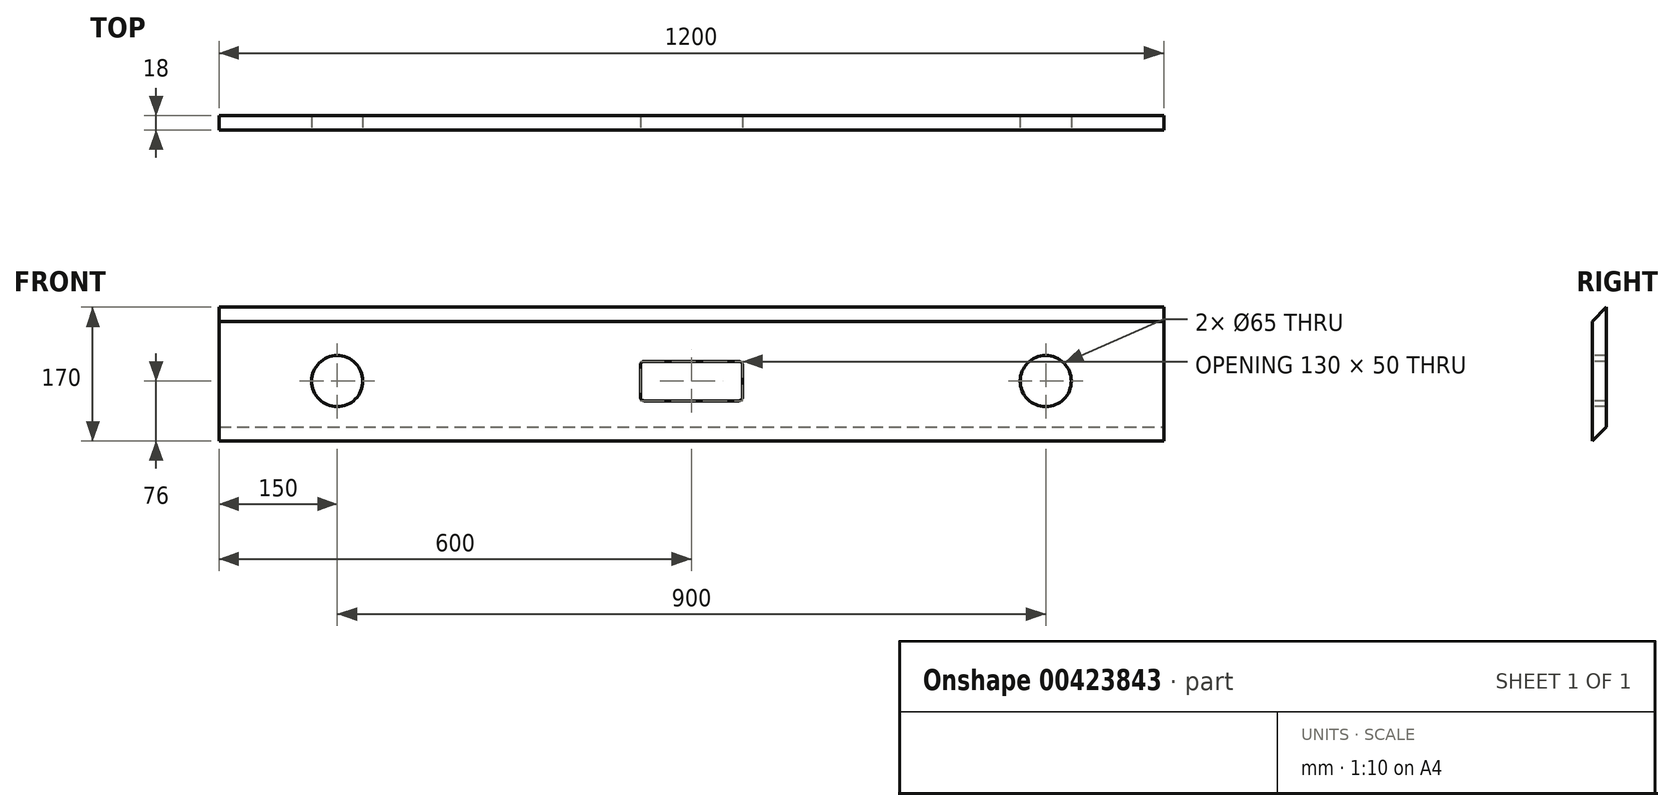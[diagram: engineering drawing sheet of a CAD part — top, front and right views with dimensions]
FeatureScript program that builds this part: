
annotation { "Feature Type Name" : "Feature", "Feature Type Description" : "" }
export const myFeature = defineFeature(function(context is Context, id is Id, definition is map)
    precondition{}
    {
        {
            var Q0;
            Q0=qCreatedBy(makeId("Front.planeOp"),FACE);
            var sketch = newSketch(context, id + "F0", { "sketchPlane" : qUnion([Q0])});
            skLineSegment(sketch, "E0.bottom", {"start": v(0, 0) * mm, "end": v(1200, 0) * mm});
            skLineSegment(sketch, "E0.top", {"start": v(0, 170) * mm, "end": v(1200, 170) * mm});
            skLineSegment(sketch, "E0.left", {"start": v(0, 0) * mm, "end": v(0, 170) * mm});
            skLineSegment(sketch, "E0.right", {"start": v(1200, 0) * mm, "end": v(1200, 170) * mm});
            skSolve(sketch);
        }
        {
            var Q0;
            Q0=qSketchRegion(id+"F0",true);
            extrude(context, id + "F1", {"entities" : qUnion([Q0]), "depth" : 18 * mm});
        }
        {
            var Q0;
            Q0=makeQuery(id+"F1.opExtrude","SWEPT_FACE",FACE,{"disambiguationData":[OSD([sQuery(id+"F0.wireOp",EDGE,"E0.right")])]});
            var sketch = newSketch(context, id + "F2", { "sketchPlane" : qUnion([Q0])});
            skLineSegment(sketch, "E1", {"start": v(0, 170) * mm, "end": v(-18, 152) * mm});
            skLineSegment(sketch, "E2", {"start": v(-18, 152) * mm, "end": v(-18, 170) * mm});
            skLineSegment(sketch, "E3", {"start": v(-18, 170) * mm, "end": v(0, 170) * mm});
            skLineSegment(sketch, "E4", {"start": v(0, 0) * mm, "end": v(0, 18) * mm});
            skLineSegment(sketch, "E5", {"start": v(0, 18) * mm, "end": v(-18, 0) * mm});
            skLineSegment(sketch, "E6", {"start": v(-18, 0) * mm, "end": v(0, 0) * mm});
            skSolve(sketch);
        }
        {
            var Q0;
            Q0=qSketchRegion(id+"F2",true);
            extrude(context, id + "F3", {"entities" : qUnion([Q0]), "operationType" : NewBodyOperationType.REMOVE, "endBound" : BoundingType.THROUGH_ALL, "oppositeDirection" : true, "depth" : 25 * mm});
        }
        {
            var Q0;
            Q0=makeQuery(id+"F1.opExtrude","CAP_FACE",FACE,{"disambiguationData":[OSD([sQuery(id+"F0.wireOp",EDGE,"E0.bottom"),sQuery(id+"F0.wireOp",EDGE,"E0.top"),sQuery(id+"F0.wireOp",EDGE,"E0.left"),sQuery(id+"F0.wireOp",EDGE,"E0.right")])],"isStart":false});
            var sketch = newSketch(context, id + "F4", { "sketchPlane" : qUnion([Q0])});
            skLineSegment(sketch, "E7", {"start": v(0, 76) * mm, "end": v(1200, 76) * mm, "construction": true});
            skLineSegment(sketch, "E8", {"start": v(600, 152) * mm, "end": v(600, 0) * mm, "construction": true});
            skCircle(sketch, "E9", {"center": v(150, 76) * mm, "radius": 32.5 * mm});
            skCircle(sketch, "E10", {"center": v(1050, 76) * mm, "radius": 32.5 * mm});
            skLineSegment(sketch, "E11.bottom", {"start": v(660, 51) * mm, "end": v(540, 51) * mm});
            skLineSegment(sketch, "E11.top", {"start": v(660, 101) * mm, "end": v(540, 101) * mm});
            skLineSegment(sketch, "E11.left", {"start": v(665, 56) * mm, "end": v(665, 96) * mm});
            skLineSegment(sketch, "E11.right", {"start": v(535, 56) * mm, "end": v(535, 96) * mm});
            skPoint(sketch, "E11.middle", {"position": v(600, 76) * mm});
            skPoint(sketch, "E12.visualSharp", {"position": v(535, 101) * mm});
            skArc(sketch, "E12.filletArc", {"start": v(540, 101) * mm, "mid": v(536.46, 99.54) * mm, "end": v(535, 96) * mm});
            skPoint(sketch, "E13.visualSharp", {"position": v(535, 51) * mm});
            skArc(sketch, "E13.filletArc", {"start": v(535, 56) * mm, "mid": v(536.46, 52.46) * mm, "end": v(540, 51) * mm});
            skPoint(sketch, "E14.visualSharp", {"position": v(665, 51) * mm});
            skArc(sketch, "E14.filletArc", {"start": v(660, 51) * mm, "mid": v(663.54, 52.46) * mm, "end": v(665, 56) * mm});
            skPoint(sketch, "E15.visualSharp", {"position": v(665, 101) * mm});
            skArc(sketch, "E15.filletArc", {"start": v(665, 96) * mm, "mid": v(663.54, 99.54) * mm, "end": v(660, 101) * mm});
            skSolve(sketch);
        }
        {
            var Q0;
            Q0=qSketchRegion(id+"F4",true);
            extrude(context, id + "F5", {"entities" : qUnion([Q0]), "operationType" : NewBodyOperationType.REMOVE, "endBound" : BoundingType.THROUGH_ALL, "oppositeDirection" : true, "depth" : 25 * mm});
        }
    });
